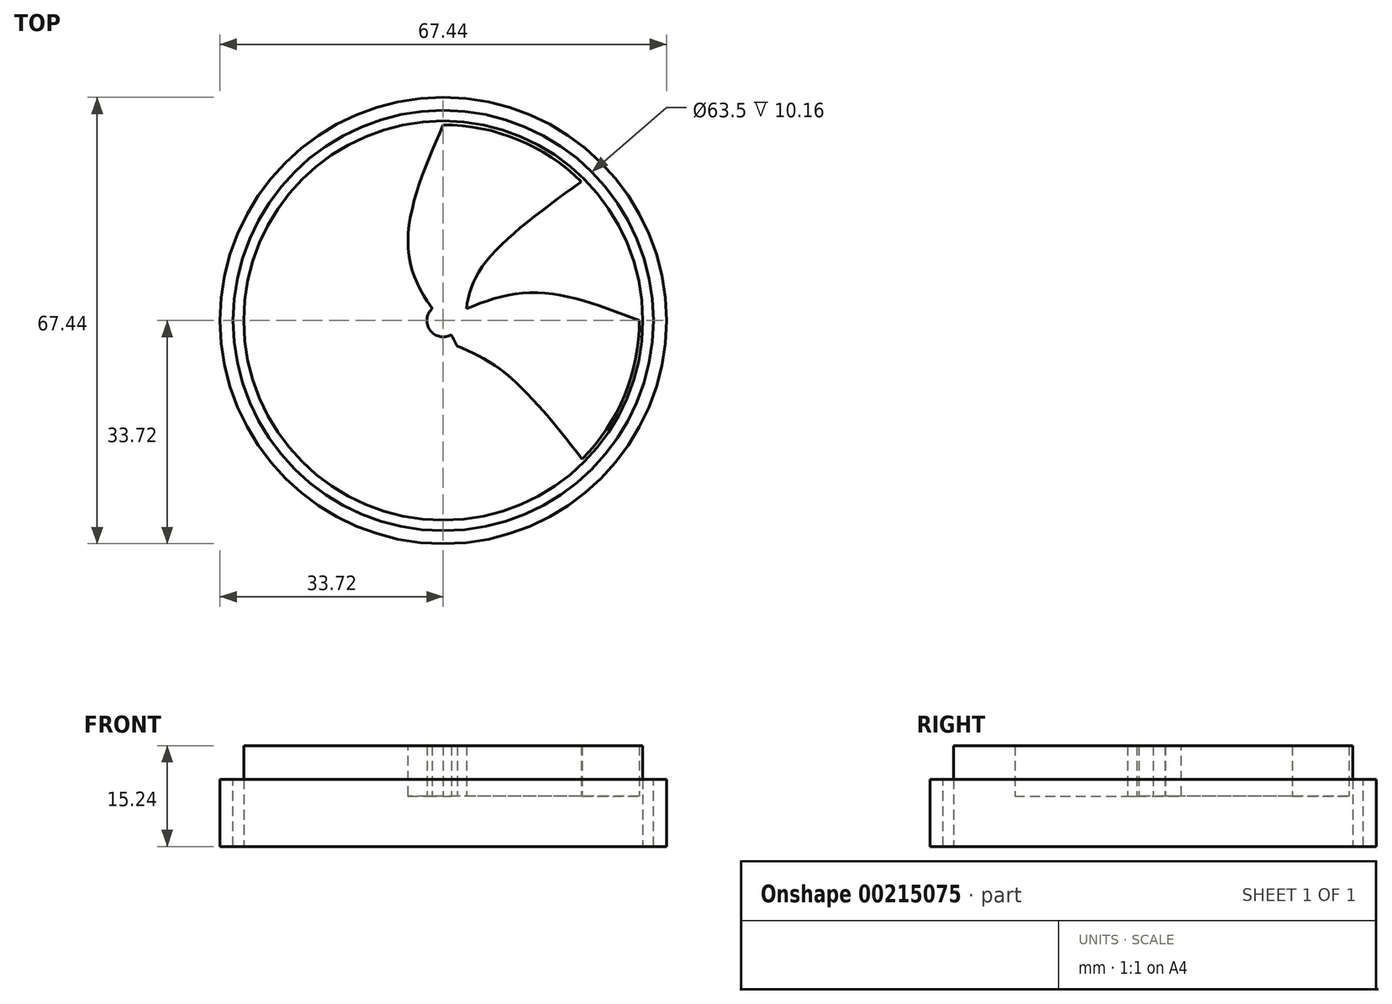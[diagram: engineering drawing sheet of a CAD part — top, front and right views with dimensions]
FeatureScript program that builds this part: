
annotation { "Feature Type Name" : "Feature", "Feature Type Description" : "" }
export const myFeature = defineFeature(function(context is Context, id is Id, definition is map)
    precondition{}
    {
        {
            var Q0;
            Q0=qCreatedBy(makeId("Top.planeOp"),FACE);
            var sketch = newSketch(context, id + "F0", { "sketchPlane" : qUnion([Q0])});
            skCircle(sketch, "E0", {"center": v(0, 0) * mm, "radius": 33.72 * mm});
            skSolve(sketch);
        }
        {
            var Q0;
            Q0=makeQuery(id+"F0.imprint","IMPRINT",FACE,{"disambiguationData":[TD([[makeQuery(id+"F0.imprint","IMPRINT",EDGE,{"derivedFrom":sQuery(id+"F0.wireOp",EDGE,"E0")}),1.0]])]});
            extrude(context, id + "F1", {"entities" : qUnion([Q0]), "depth" : 10.16 * mm});
        }
        {
            var Q0;
            Q0=makeQuery(id+"F1.opExtrude","CAP_FACE",FACE,{"disambiguationData":[OSD([sQuery(id+"F0.wireOp",EDGE,"E0")])],"isStart":false});
            var sketch = newSketch(context, id + "F2", { "sketchPlane" : qUnion([Q0])});
            skCircle(sketch, "E1", {"center": v(0, 0) * mm, "radius": 31.8 * mm});
            skSolve(sketch);
        }
        {
            var Q0;
            Q0=sQuery(id+"F2.wireOp",VERTEX,"E1.center");
            var Q1;
            Q1=makeQuery(id+"F1.opExtrude","SWEPT_BODY",BODY,{"disambiguationData":[OSD([sQuery(id+"F0.wireOp",EDGE,"E0")])]});
            hole(context, id + "F3", {"style" : HoleStyle.SIMPLE, "endStyle" : HoleEndStyle.THROUGH, "holeDiameter" : 63.5 * mm, "locations" : qUnion([Q0]), "scope" : qUnion([Q1]), "isTappedThrough" : true});
        }
        {
            var Q0;
            Q0=qCreatedBy(makeId("Top.planeOp"),FACE);
            var sketch = newSketch(context, id + "F4", { "sketchPlane" : qUnion([Q0])});
            skCircle(sketch, "E2", {"center": v(0, 0) * mm, "radius": 30.16 * mm});
            skSolve(sketch);
        }
        {
            var Q0;
            Q0=makeQuery(id+"F4.imprint","IMPRINT",FACE,{"disambiguationData":[TD([[makeQuery(id+"F4.imprint","IMPRINT",EDGE,{"derivedFrom":sQuery(id+"F4.wireOp",EDGE,"E2")}),1.0]])]});
            var sketch = newSketch(context, id + "F9", { "sketchPlane" : qUnion([Q0])});
            skSolve(sketch);
        }
        {
            var Q0;
            Q0 = qSketchRegion(id + "F9", true);
            var Q1;
            Q1=makeQuery(id+"F9.imprint","IMPRINT",FACE,{"disambiguationData":[TD([[makeQuery(id+"F9.imprint","IMPRINT",EDGE,{"derivedFrom":makeQuery(id+"F4.imprint","IMPRINT",EDGE,{"derivedFrom":sQuery(id+"F4.wireOp",EDGE,"E2")})}),1.0]])]});
            extrude(context, id + "F5", {"entities" : qUnion([Q0, Q1]), "depth" : 7.62 * mm});
        }
        {
            var Q0;
            Q0=makeQuery(id+"F5.opExtrude","CAP_FACE",FACE,{"disambiguationData":[OSD([sQuery(id+"F4.wireOp",EDGE,"E2")])],"isStart":false});
            var sketch = newSketch(context, id + "F6", { "sketchPlane" : qUnion([Q0])});
            skCircle(sketch, "E3", {"center": v(0, 0) * mm, "radius": 2.47 * mm});
            skSolve(sketch);
        }
        {
            var Q0;
            Q0=makeQuery(id+"F6.imprint","IMPRINT",FACE,{"disambiguationData":[TD([[makeQuery(id+"F6.imprint","IMPRINT",EDGE,{"derivedFrom":sQuery(id+"F6.wireOp",EDGE,"E3")}),-1.0]])]});
            var sketch = newSketch(context, id + "F7", { "sketchPlane" : qUnion([Q0])});
            skArc(sketch, "E4", {"start": v(0, 29.57) * mm, "mid": v(11.27, 27.34) * mm, "end": v(20.84, 20.98) * mm});
            skArc(sketch, "E5", {"start": v(29.64, 0) * mm, "mid": v(27.4, -11.32) * mm, "end": v(21, -20.93) * mm});
            skArc(sketch, "E6", {"start": v(0, -29.77) * mm, "mid": v(-11.32, -27.54) * mm, "end": v(-20.93, -21.17) * mm});
            skArc(sketch, "E7", {"start": v(-29.92, 0) * mm, "mid": v(-27.51, 11.75) * mm, "end": v(-20.69, 21.6) * mm});
            skFitSpline(sketch, "E8", {"points": [v(-29.1, -0.49) * mm, v(-11.97, -6.1) * mm, v(0, 0) * mm, v(0, 0) * mm, v(0, 0) * mm], "startDerivative": vector(33.56, -16.8) * mm, "endDerivative": vector(24.42, 18.63) * mm});
            skFitSpline(sketch, "E9", {"points": [v(-20.69, 21.6) * mm, v(-7.5, 4.34) * mm, v(0, 3.01) * mm], "startDerivative": vector(21.26, -35) * mm, "endDerivative": vector(20.01, 0.88) * mm});
            skFitSpline(sketch, "E10", {"points": [v(0, 29.57) * mm, v(-5.04, 8.88) * mm, v(0, 0) * mm, v(0.62, -0.37) * mm], "startDerivative": vector(-17.82, -41.02) * mm, "endDerivative": vector(4.95, -1.83) * mm});
            skFitSpline(sketch, "E11", {"points": [v(20.84, 20.98) * mm, v(5.46, 7.48) * mm, v(3.25, -0.37) * mm], "startDerivative": vector(-31.02, -22.56) * mm, "endDerivative": vector(-1.97, -19.96) * mm});
            skFitSpline(sketch, "E12", {"points": [v(29.64, 0) * mm, v(13.18, 4.2) * mm, v(-0.2, 0.13) * mm], "startDerivative": vector(-32.25, 12.38) * mm, "endDerivative": vector(-27.34, -12.52) * mm});
            skFitSpline(sketch, "E13", {"points": [v(21, -20.93) * mm, v(9.04, -7.7) * mm, v(0.37, -3.18) * mm], "startDerivative": vector(-20.93, 26.6) * mm, "endDerivative": vector(-20.3, 7.98) * mm});
            skFitSpline(sketch, "E14", {"points": [v(0, -29.77) * mm, v(4.27, -11.24) * mm, v(0, 0) * mm], "startDerivative": vector(12.48, 35.46) * mm, "endDerivative": vector(-13.47, 23.64) * mm});
            skFitSpline(sketch, "E15", {"points": [v(-20.93, -21.17) * mm, v(-4.6, -9.47) * mm, v(-3.2, 0.13) * mm], "startDerivative": vector(34.86, 18.78) * mm, "endDerivative": vector(-1.57, 24.15) * mm});
            skFitSpline(sketch, "E16", {"points": [v(-29.92, 0) * mm, v(-29.1, -0.49) * mm], "startDerivative": vector(0.82, -0.49) * mm, "endDerivative": vector(0.82, -0.49) * mm});
            skSolve(sketch);
        }
        {
            var Q0;
            {var subQ5=sQuery(id+"F7.wireOp",EDGE,"E4");Q0=makeQuery(id+"F7.imprint","IMPRINT",FACE,{"disambiguationData":[TD([[makeQuery(id+"F7.imprint","IMPRINT",EDGE,{"derivedFrom":subQ5}),-1.0]])]});}
            var Q1;
            {var subQ5=sQuery(id+"F7.wireOp",EDGE,"E5");Q1=makeQuery(id+"F7.imprint","IMPRINT",FACE,{"disambiguationData":[TD([[makeQuery(id+"F7.imprint","IMPRINT",EDGE,{"derivedFrom":subQ5}),-1.0]])]});}
            var Q2;
            {var subQ4=sQuery(id+"F7.wireOp",EDGE,"E7");Q2=makeQuery(id+"F7.imprint","IMPRINT",FACE,{"disambiguationData":[TD([[makeQuery(id+"F7.imprint","IMPRINT",EDGE,{"derivedFrom":subQ4}),-1.0]])]});}
            var Q3;
            {var subQ1=sQuery(id+"F7.wireOp",EDGE,"E6");Q3=makeQuery(id+"F7.imprint","IMPRINT",FACE,{"disambiguationData":[TD([[makeQuery(id+"F7.imprint","IMPRINT",EDGE,{"derivedFrom":subQ1}),-1.0]])]});}
            extrude(context, id + "F8", {"entities" : qUnion([Q0, Q1, Q2, Q3]), "operationType" : NewBodyOperationType.ADD, "depth" : 7.62 * mm});
        }
    });
